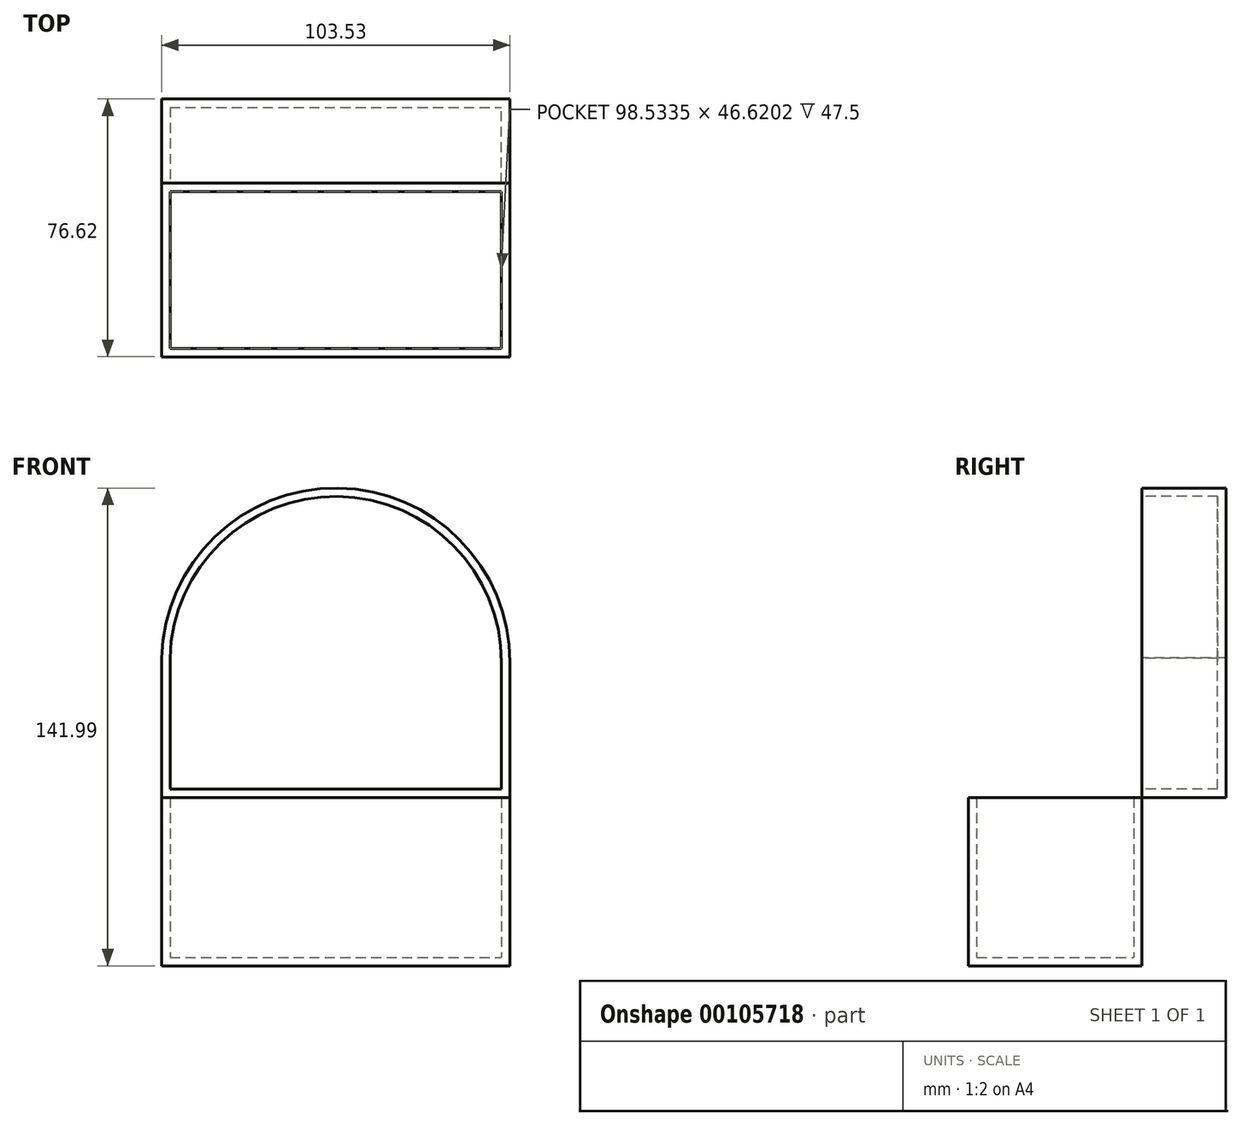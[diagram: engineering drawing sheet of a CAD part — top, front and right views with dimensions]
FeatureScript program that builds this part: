
annotation { "Feature Type Name" : "Feature", "Feature Type Description" : "" }
export const myFeature = defineFeature(function(context is Context, id is Id, definition is map)
    precondition{}
    {
        {
            var Q0;
            Q0=qCreatedBy(makeId("Top.planeOp"),FACE);
            var sketch = newSketch(context, id + "F0", { "sketchPlane" : qUnion([Q0])});
            skLineSegment(sketch, "E0.bottom", {"start": v(-49.86, -22.14) * mm, "end": v(53.67, -22.14) * mm});
            skLineSegment(sketch, "E0.top", {"start": v(-49.86, 29.48) * mm, "end": v(53.67, 29.48) * mm});
            skLineSegment(sketch, "E0.left", {"start": v(-49.86, -22.14) * mm, "end": v(-49.86, 29.48) * mm});
            skLineSegment(sketch, "E0.right", {"start": v(53.67, -22.14) * mm, "end": v(53.67, 29.48) * mm});
            skSolve(sketch);
        }
        {
            var Q0;
            Q0=makeQuery(id+"F0.imprint","IMPRINT",FACE,{"disambiguationData":[TD([[makeQuery(id+"F0.imprint","IMPRINT",EDGE,{"derivedFrom":sQuery(id+"F0.wireOp",EDGE,"E0.bottom")}),1.0]])]});
            extrude(context, id + "F1", {"entities" : qUnion([Q0]), "depth" : 50 * mm});
        }
        {
            var Q0;
            Q0=makeQuery(id+"F1.opExtrude","CAP_FACE",FACE,{"disambiguationData":[OSD([sQuery(id+"F0.wireOp",EDGE,"E0.bottom"),sQuery(id+"F0.wireOp",EDGE,"E0.top"),sQuery(id+"F0.wireOp",EDGE,"E0.left"),sQuery(id+"F0.wireOp",EDGE,"E0.right")])],"isStart":false});
            shell(context, id + "F2", {"entities" : qUnion([Q0]), "thickness" : 2.5 * mm});
        }
        {
            var Q0;
            Q0=makeQuery(id+"F1.opExtrude","SWEPT_FACE",FACE,{"disambiguationData":[OSD([sQuery(id+"F0.wireOp",EDGE,"E0.top")])]});
            var sketch = newSketch(context, id + "F3", { "sketchPlane" : qUnion([Q0])});
            skLineSegment(sketch, "E1", {"start": v(-53.67, 50) * mm, "end": v(-53.67, 90.22) * mm});
            skLineSegment(sketch, "E2", {"start": v(49.86, 50) * mm, "end": v(49.86, 91.46) * mm});
            skArc(sketch, "E3", {"start": v(49.86, 91.46) * mm, "mid": v(-2.52, 141.99) * mm, "end": v(-53.67, 90.22) * mm});
            skSolve(sketch);
        }
        {
            var Q0;
            Q0=makeQuery(id+"F3.imprint","IMPRINT",FACE,{"disambiguationData":[TD([[makeQuery(id+"F3.imprint","IMPRINT",EDGE,{"derivedFrom":sQuery(id+"F3.wireOp",EDGE,"E1")}),-1.0]])]});
            extrude(context, id + "F4", {"entities" : qUnion([Q0]), "depth" : 25 * mm});
        }
        {
            var Q0;
            Q0=makeQuery(id+"F4.opExtrude","CAP_FACE",FACE,{"disambiguationData":[OSD([sQuery(id+"F0.wireOp",EDGE,"E0.top"),sQuery(id+"F3.wireOp",EDGE,"E1"),sQuery(id+"F3.wireOp",EDGE,"E2"),sQuery(id+"F3.wireOp",EDGE,"E3")])],"isStart":true});
            shell(context, id + "F5", {"entities" : qUnion([Q0]), "thickness" : 2.5 * mm});
        }
    });
